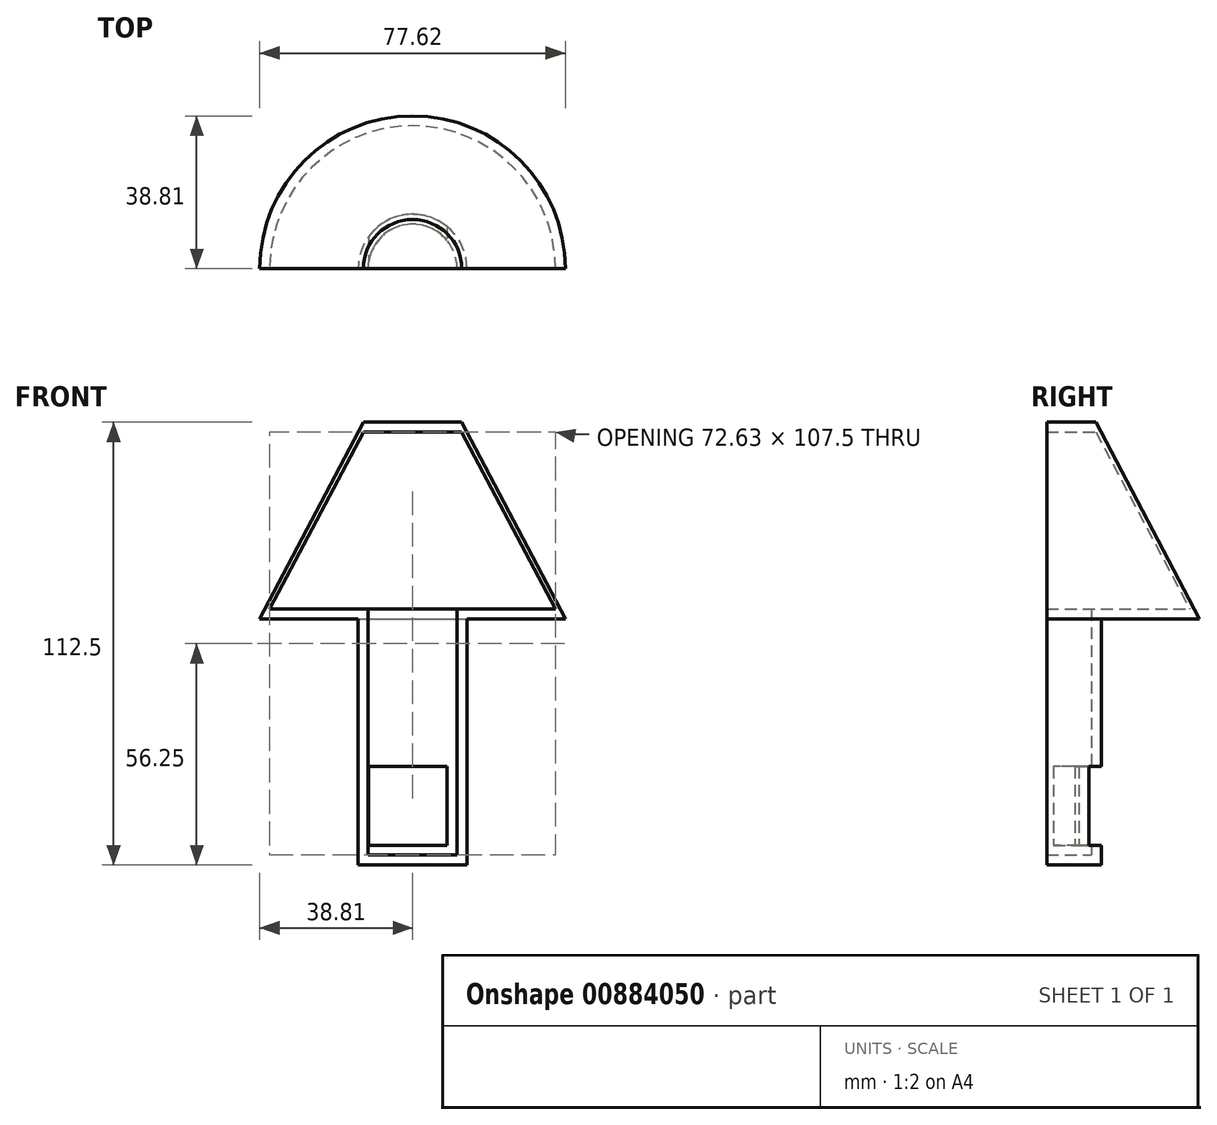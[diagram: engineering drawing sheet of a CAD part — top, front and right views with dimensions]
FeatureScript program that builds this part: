
annotation { "Feature Type Name" : "Feature", "Feature Type Description" : "" }
export const myFeature = defineFeature(function(context is Context, id is Id, definition is map)
    precondition{}
    {
        {
            var Q0;
            Q0=qCreatedBy(makeId("Right.planeOp"),FACE);
            var sketch = newSketch(context, id + "F0", { "sketchPlane" : qUnion([Q0])});
            skLineSegment(sketch, "E0", {"start": v(0, -62.5) * mm, "end": v(13.81, -62.5) * mm});
            skLineSegment(sketch, "E1", {"start": v(13.81, -62.5) * mm, "end": v(13.81, 0) * mm});
            skLineSegment(sketch, "E2", {"start": v(13.81, 0) * mm, "end": v(38.81, 0) * mm});
            skLineSegment(sketch, "E3", {"start": v(0, 50) * mm, "end": v(12.5, 50) * mm});
            skLineSegment(sketch, "E4", {"start": v(12.5, 50) * mm, "end": v(38.81, 0) * mm});
            skLineSegment(sketch, "E5", {"start": v(0, -62.5) * mm, "end": v(0, -60) * mm});
            skLineSegment(sketch, "E6", {"start": v(0, -60) * mm, "end": v(11.31, -60) * mm});
            skLineSegment(sketch, "E7", {"start": v(11.31, 2.5) * mm, "end": v(36.31, 2.5) * mm});
            skLineSegment(sketch, "E8", {"start": v(0, 50) * mm, "end": v(0, 47.5) * mm});
            skLineSegment(sketch, "E9", {"start": v(0, 47.5) * mm, "end": v(12.5, 47.5) * mm});
            skLineSegment(sketch, "E10", {"start": v(12.5, 47.5) * mm, "end": v(36.31, 2.5) * mm});
            skPoint(sketch, "E11.start.orphan", {"position": v(11.31, 0) * mm});
            skLineSegment(sketch, "E12", {"start": v(11.31, -60) * mm, "end": v(11.31, 2.5) * mm});
            skSolve(sketch);
        }
        {
            var Q0;
            Q0=makeQuery(id+"F0.imprint","IMPRINT",FACE,{"disambiguationData":[TD([[makeQuery(id+"F0.imprint","IMPRINT",EDGE,{"derivedFrom":sQuery(id+"F0.wireOp",EDGE,"E0")}),1.0]])]});
            var Q1;
            Q1=sQuery(id+"F0.wireOp",EDGE,"E5");
            revolve(context, id + "F1", {"surfaceOperationType" : NewSurfaceOperationType.NEW, "entities" : qUnion([Q0]), "axis" : qUnion([Q1]), "revolveType" : RevolveType.SYMMETRIC, "angle" : 180 * degree});
        }
        {
            var Q0;
            Q0=qCreatedBy(makeId("Front.planeOp"),FACE);
            var sketch = newSketch(context, id + "F2", { "sketchPlane" : qUnion([Q0])});
            skLineSegment(sketch, "E13", {"start": v(8.81, -57.5) * mm, "end": v(8.81, -37.5) * mm});
            skLineSegment(sketch, "E14", {"start": v(8.81, -37.5) * mm, "end": v(-11.19, -37.5) * mm});
            skLineSegment(sketch, "E15", {"start": v(-11.19, -37.5) * mm, "end": v(-11.19, -57.5) * mm});
            skLineSegment(sketch, "E16", {"start": v(-11.19, -57.5) * mm, "end": v(8.81, -57.5) * mm});
            skSolve(sketch);
        }
        {
            var Q0;
            Q0=makeQuery(id+"F2.imprint","IMPRINT",FACE,{"disambiguationData":[TD([[makeQuery(id+"F2.imprint","IMPRINT",EDGE,{"derivedFrom":sQuery(id+"F2.wireOp",EDGE,"E13")}),1.0]])]});
            extrude(context, id + "F3", {"entities" : qUnion([Q0]), "operationType" : NewBodyOperationType.REMOVE, "oppositeDirection" : true, "depth" : 25 * mm, "offsetDistance" : 25 * mm});
        }
    });
